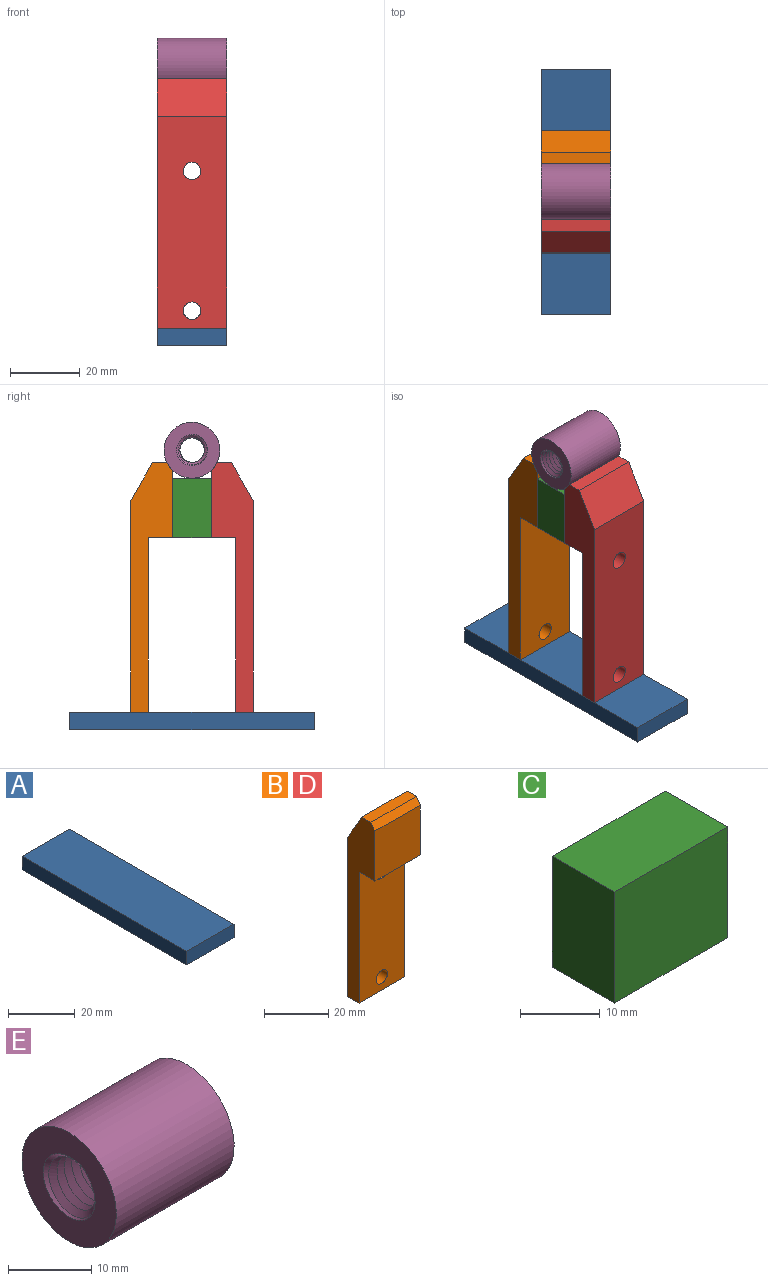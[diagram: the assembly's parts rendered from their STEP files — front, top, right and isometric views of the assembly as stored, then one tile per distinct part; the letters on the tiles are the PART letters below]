
ASSEMBLY  parts=5 mates=4
PART A: 6 faces, bbox 20x70x5 mm
  f0: plane 70x20mm, normal (0,0,1), area 1400mm2, adj f1,f3,f4,f5
  f1: plane 20x5mm, normal (0,-1,0), area 100mm2, adj f0,f2,f4,f5
  f2: plane 70x20mm, normal (0,0,-1), area 1400mm2, adj f1,f3,f4,f5
  f3: plane 20x5mm, normal (0,1,0), area 100mm2, adj f0,f2,f4,f5
  f4: plane 70x5mm, normal (1,0,0), area 350mm2, adj f0,f1,f2,f3
  f5: plane 70x5mm, normal (-1,0,0), area 350mm2, adj f0,f1,f2,f3
PART B: 12 faces, bbox 20x12x71.4 mm
  f0: plane 60.69x20mm, normal (0,1,0), area 1174.5mm2, adj f1,f7,f8,f9,f10,f11
  f1: plane 20x10.71mm, normal (0,0.87,0.5), area 247.4mm2, adj f0,f2,f8,f9
  f2: plane 20x4.02mm, normal (0,0,1), area 80.3mm2, adj f1,f3,f8,f9
  f3: plane 20x2.4mm, normal (0,-0.8,0.6), area 60mm2, adj f2,f4,f8,f9
  f4: plane 20x19mm, normal (0,-1,0), area 380mm2, adj f3,f5,f8,f9
  f5: plane 20x7mm, normal (0,0,-1), area 140mm2, adj f4,f6,f8,f9
  f6: plane 50x20mm, normal (0,-1,0), area 960.7mm2, adj f5,f7,f8,f9,f10,f11
  f7: plane 20x5mm, normal (0,0,-1), area 100mm2, adj f0,f6,f8,f9
  f8: plane 71.4x12mm, normal (1,0,0), area 471.5mm2, adj f0,f1,f2,f3,f4,f5,f6,f7
  f9: plane 71.4x12mm, normal (-1,0,0), area 471.5mm2, adj f0,f1,f2,f3,f4,f5,f6,f7
  f10: cylinder r=2.5mm len=5mm, axis (0,1,0), area 78.5mm2, adj f0,f6
  f11: cylinder r=2.5mm len=5mm, axis (0,1,0), area 78.5mm2, adj f0,f6
PART C: 6 faces, bbox 20x11x17 mm
  f0: plane 20x17mm, normal (0,1,0), area 340mm2, adj f1,f3,f4,f5
  f1: plane 20x11mm, normal (0,0,1), area 220mm2, adj f0,f2,f4,f5
  f2: plane 20x17mm, normal (0,-1,0), area 340mm2, adj f1,f3,f4,f5
  f3: plane 20x11mm, normal (0,0,-1), area 220mm2, adj f0,f2,f4,f5
  f4: plane 17x11mm, normal (1,0,0), area 187mm2, adj f0,f1,f2,f3
  f5: plane 17x11mm, normal (-1,0,0), area 187mm2, adj f0,f1,f2,f3
PART D: same geometry as B
PART E: 10 faces, bbox 20.8x16.1x16.1 mm
  f0: cylinder r=3.4mm len=3.24mm, axis (-1,0,0), area 0.5mm2, adj f1,f8,f9
  f1: cone r=4.4mm half-angle=45deg, axis (1,0,0), area 26.5mm2, adj f0,f3,f6,f8,f9
  f2: cylinder r=8mm len=20mm, axis (-1,0,0), area 1005.3mm2, adj f3,f4
  f3: plane 16x16mm, normal (1,0,0), area 140.2mm2, adj f1,f2
  f4: plane 16.06x16.06mm, normal (-1,0,0), area 139.7mm2, adj f2,f5,f6,f7
  f5: cone r=3.4mm half-angle=45deg, axis (-1,0,0), area 12.7mm2, adj f4,f6,f7
  f6: bspline ~20.21x10.65mm, area 487.6mm2, adj f1,f4,f5,f7,f8,f9
  f7: bspline ~20x10.65mm, area 479.5mm2, adj f4,f5,f6,f8
  f8: plane 1.21x0.96mm, normal (0,-1,0), area 0.5mm2, adj f0,f1,f6,f7,f9
  f9: bspline ~7.06x4.08mm, area 0.9mm2, adj f0,f1,f6,f8
PLACE A t=(-10,0,30)mm fixed
PLACE B t=(-10,0,30)mm
PLACE C t=(-10,0,30)mm
PLACE D rot(axis=(0,0,1),180deg) t=(10,0,30)mm
PLACE E t=(-10,0,30)mm
MATE fastened B.f5 <-> C.f3  axis (0,0,1) through (-10,5.5,55)mm
MATE fastened D.f7 <-> A.f0  axis (0,0,-1) through (0,-15,5)mm
MATE fastened E.f4 <-> C.f5  axis (-1,0,0) through (-10,0.01,79.98)mm
MATE fastened B.f7 <-> A.f0  axis (0,0,-1) through (0,15,5)mm
